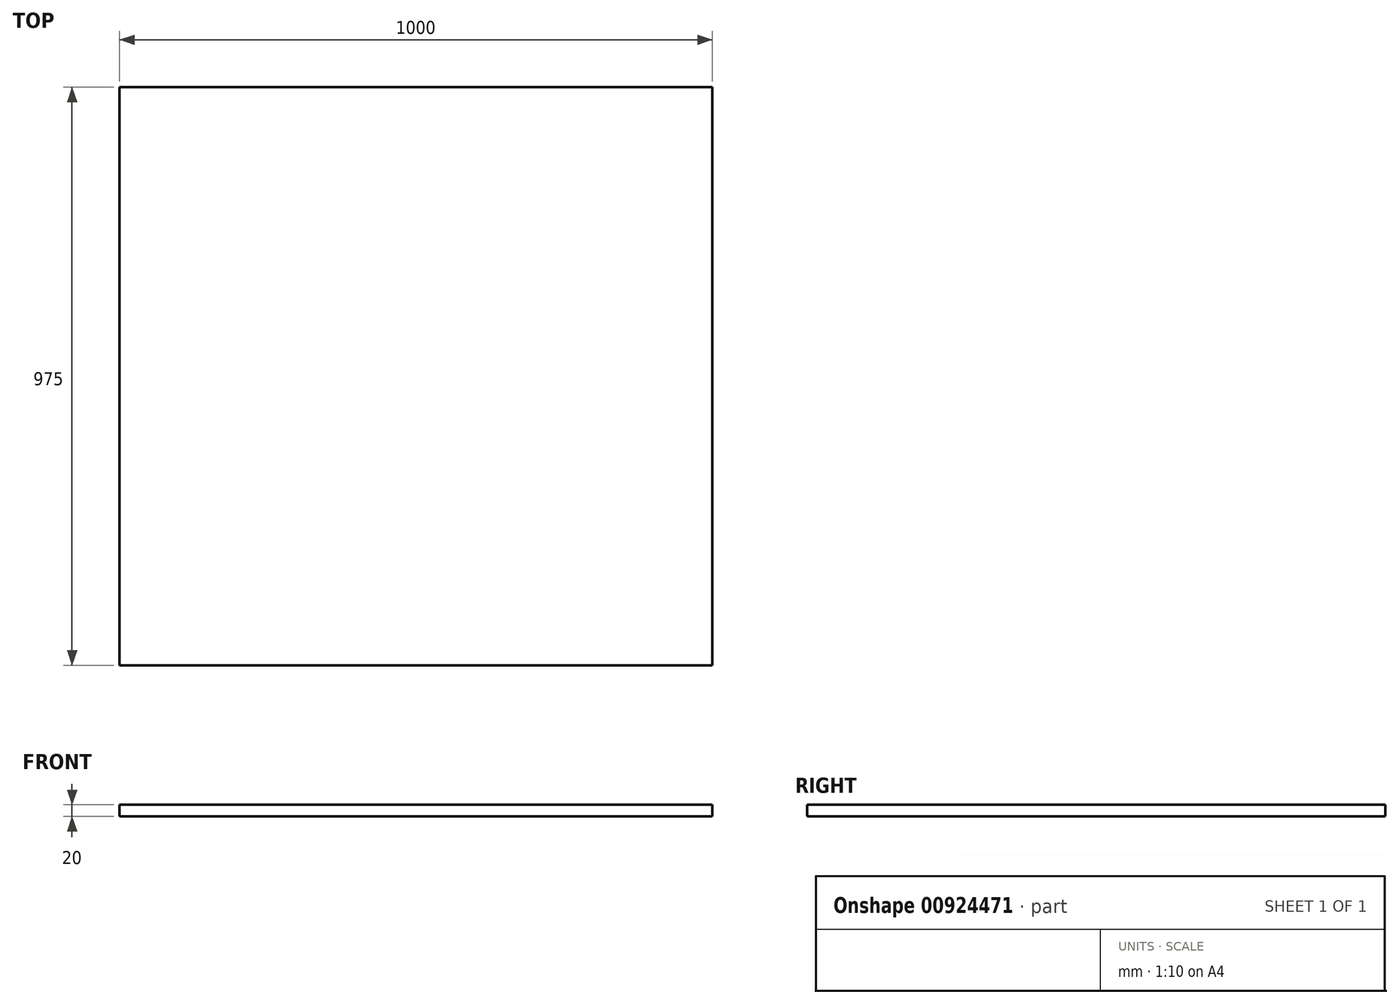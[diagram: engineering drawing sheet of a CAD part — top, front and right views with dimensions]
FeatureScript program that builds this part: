
annotation { "Feature Type Name" : "Feature", "Feature Type Description" : "" }
export const myFeature = defineFeature(function(context is Context, id is Id, definition is map)
    precondition{}
    {
        {
            var Q0;
            Q0=qCreatedBy(makeId("Front.planeOp"),FACE);
            var sketch = newSketch(context, id + "F0", { "sketchPlane" : qUnion([Q0])});
            skLineSegment(sketch, "E0.bottom", {"start": v(500, -10) * mm, "end": v(-500, -10) * mm});
            skLineSegment(sketch, "E0.top", {"start": v(500, 10) * mm, "end": v(-500, 10) * mm});
            skLineSegment(sketch, "E0.left", {"start": v(500, -10) * mm, "end": v(500, 10) * mm});
            skLineSegment(sketch, "E0.right", {"start": v(-500, -10) * mm, "end": v(-500, 10) * mm});
            skPoint(sketch, "E0.middle", {"position": v(0, 0) * mm});
            skSolve(sketch);
        }
        {
            var Q0;
            Q0=makeQuery(id+"F0.imprint","IMPRINT",FACE,{"disambiguationData":[TD([[makeQuery(id+"F0.imprint","IMPRINT",EDGE,{"derivedFrom":sQuery(id+"F0.wireOp",EDGE,"E0.bottom")}),-1.0]])]});
            extrude(context, id + "F1", {"entities" : qUnion([Q0]), "depth" : 975 * mm, "offsetDistance" : 25 * mm});
        }
    });
